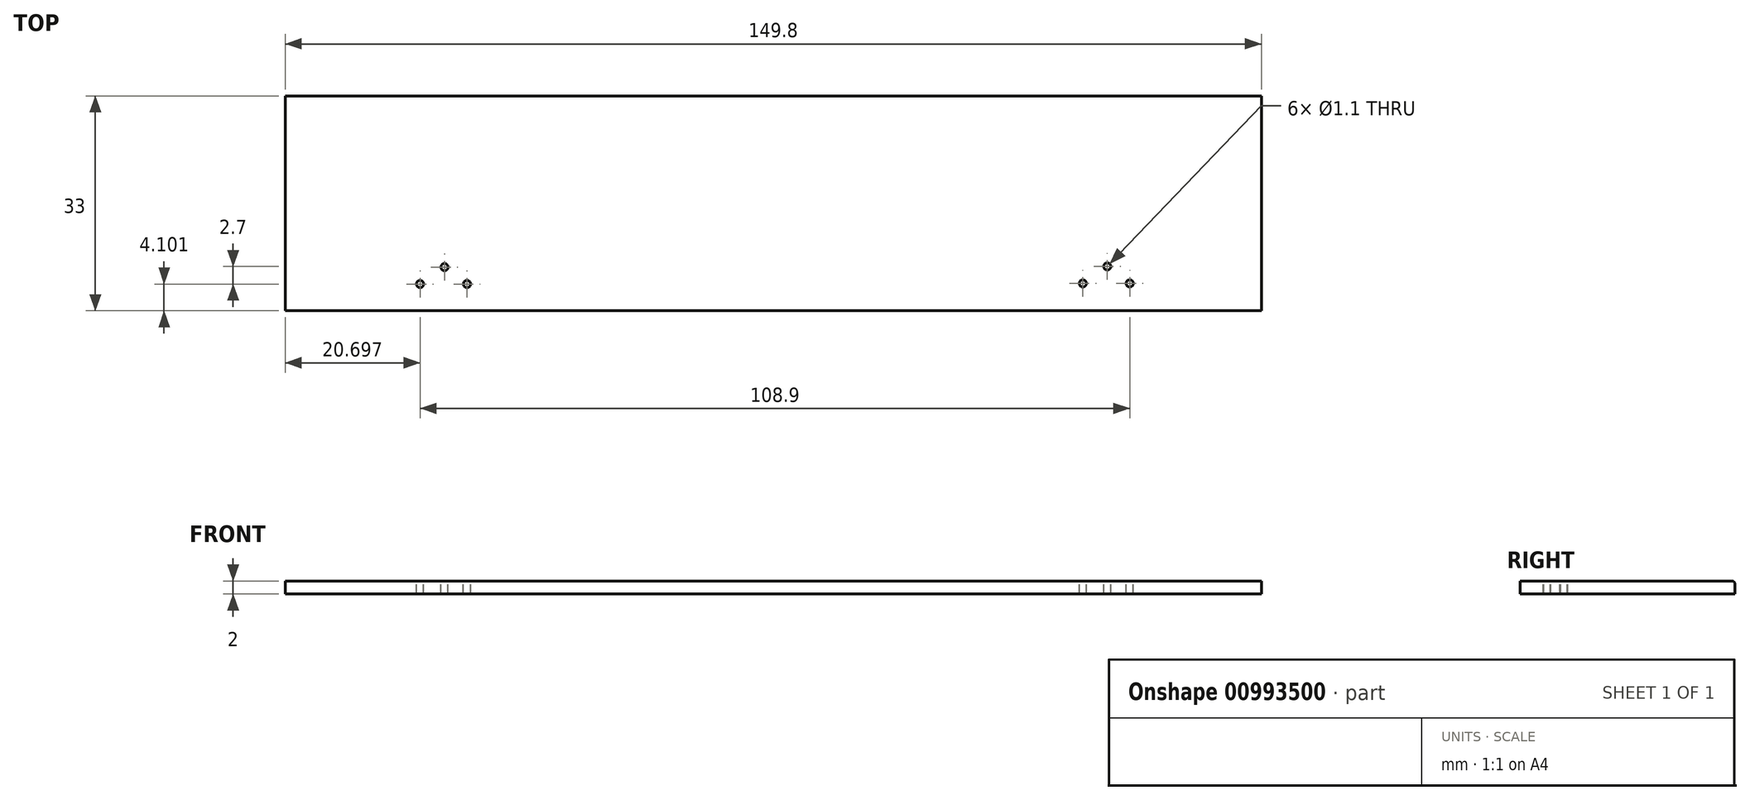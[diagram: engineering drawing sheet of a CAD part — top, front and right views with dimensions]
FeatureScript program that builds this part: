
annotation { "Feature Type Name" : "Feature", "Feature Type Description" : "" }
export const myFeature = defineFeature(function(context is Context, id is Id, definition is map)
    precondition{}
    {
        {
            var Q0;
            Q0=qCreatedBy(makeId("Top.planeOp"),FACE);
            var sketch = newSketch(context, id + "F0", { "sketchPlane" : qUnion([Q0])});
            skLineSegment(sketch, "E0.bottom", {"start": v(-85.72, 36.88) * mm, "end": v(64.08, 36.88) * mm});
            skLineSegment(sketch, "E0.top", {"start": v(-85.72, 3.88) * mm, "end": v(64.08, 3.88) * mm});
            skLineSegment(sketch, "E0.left", {"start": v(-85.72, 36.88) * mm, "end": v(-85.72, 3.88) * mm});
            skLineSegment(sketch, "E0.right", {"start": v(64.08, 36.88) * mm, "end": v(64.08, 3.88) * mm});
            skPoint(sketch, "E1", {"position": v(-65.02, 7.98) * mm});
            skPoint(sketch, "E2", {"position": v(-57.82, 7.98) * mm});
            skPoint(sketch, "E3", {"position": v(-61.27, 10.58) * mm});
            skPoint(sketch, "E4", {"position": v(43.88, 8.08) * mm});
            skPoint(sketch, "E5", {"position": v(36.68, 8.08) * mm});
            skPoint(sketch, "E6", {"position": v(40.43, 10.68) * mm});
            skSolve(sketch);
        }
        {
            var Q0;
            Q0=makeQuery(id+"F0.imprint","IMPRINT",FACE,{"disambiguationData":[TD([[makeQuery(id+"F0.imprint","IMPRINT",EDGE,{"derivedFrom":sQuery(id+"F0.wireOp",EDGE,"E0.bottom")}),-1.0]])]});
            extrude(context, id + "F1", {"entities" : qUnion([Q0]), "oppositeDirection" : true, "depth" : 2 * mm, "offsetDistance" : 25 * mm});
        }
        {
            var Q0;
            Q0=sQuery(id+"F0.wireOp",VERTEX,"E1");
            var Q1;
            Q1=sQuery(id+"F0.wireOp",VERTEX,"E3");
            var Q2;
            Q2=sQuery(id+"F0.wireOp",VERTEX,"E2");
            var Q3;
            Q3=sQuery(id+"F0.wireOp",VERTEX,"E5");
            var Q4;
            Q4=sQuery(id+"F0.wireOp",VERTEX,"E6");
            var Q5;
            Q5=sQuery(id+"F0.wireOp",VERTEX,"E4");
            var Q6;
            Q6=makeQuery(id+"F1.opExtrude","SWEPT_BODY",BODY,{"disambiguationData":[OSD([sQuery(id+"F0.wireOp",EDGE,"E0.bottom"),sQuery(id+"F0.wireOp",EDGE,"E0.top"),sQuery(id+"F0.wireOp",EDGE,"E0.left"),sQuery(id+"F0.wireOp",EDGE,"E0.right")])]});
            hole(context, id + "F2", {"style" : HoleStyle.SIMPLE, "endStyle" : HoleEndStyle.THROUGH, "holeDiameter" : 1.1 * mm, "majorDiameter" : 5 * mm, "isTappedThrough" : true, "tappedDepth" : 12 * mm, "tapClearance" : 3, "locations" : qUnion([Q0, Q1, Q2, Q3, Q4, Q5]), "scope" : qUnion([Q6])});
        }
        {
            var Q0;
            Q0=makeQuery(id+"F1.opExtrude","CAP_EDGE",EDGE,{"disambiguationData":[OSD([sQuery(id+"F0.wireOp",EDGE,"E0.bottom")])],"isStart":true});
            fillet(context, id + "F3", {"entities" : qUnion([Q0]), "radius" : 0.5 * mm, "tangentPropagation" : true, "allowEdgeOverflow" : false});
        }
    });
